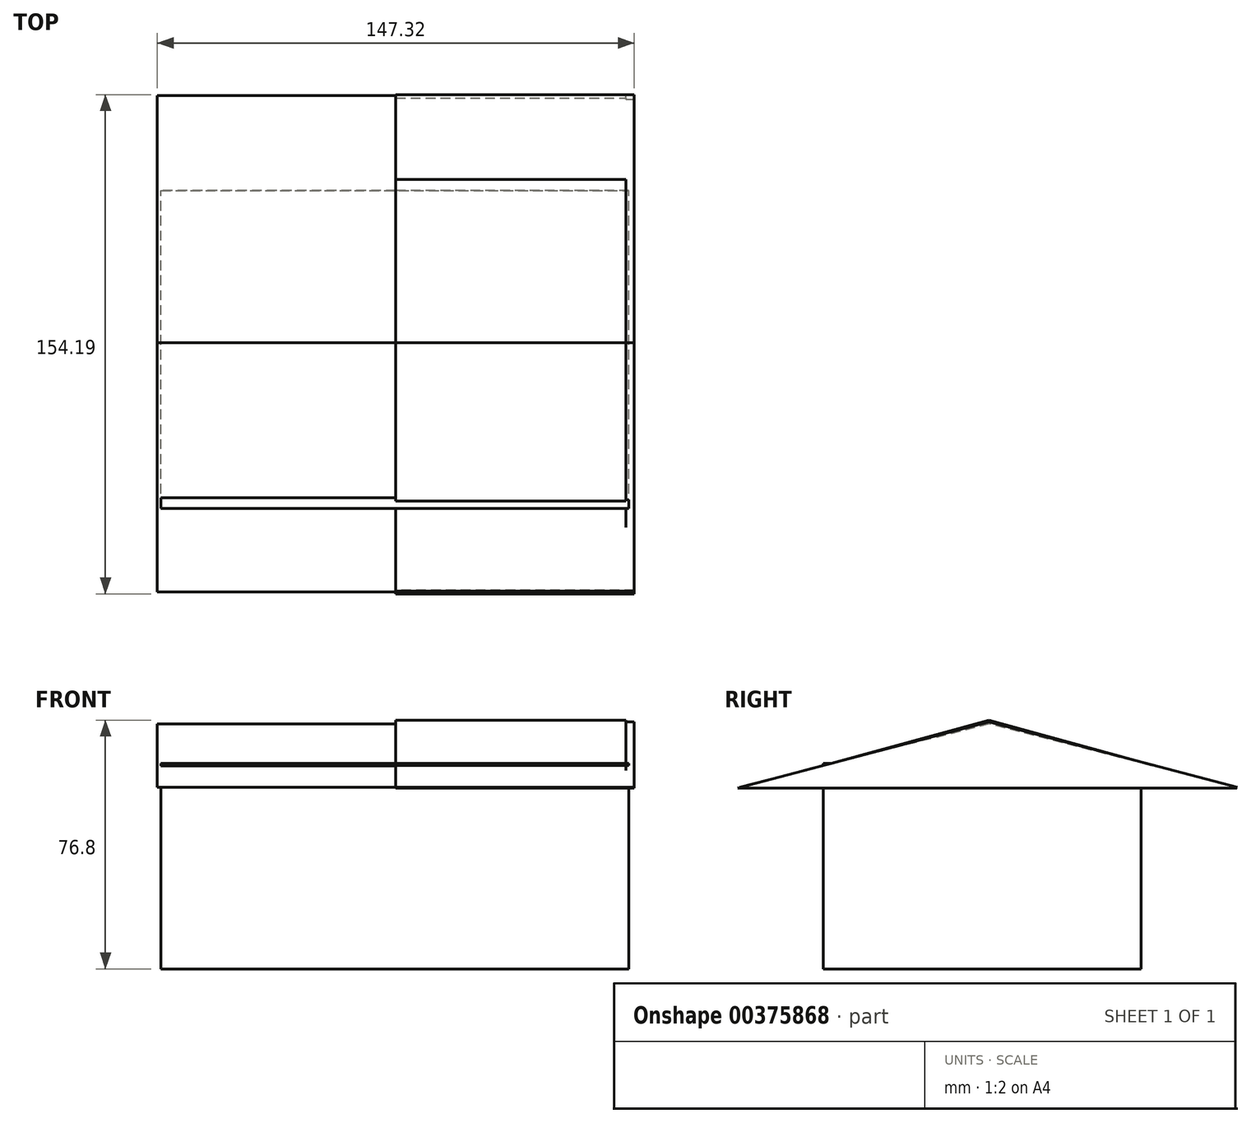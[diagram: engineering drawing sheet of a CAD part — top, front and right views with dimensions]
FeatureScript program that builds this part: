
annotation { "Feature Type Name" : "Feature", "Feature Type Description" : "" }
export const myFeature = defineFeature(function(context is Context, id is Id, definition is map)
    precondition{}
    {
        {
            var Q0;
            Q0=qCreatedBy(makeId("Top.planeOp"),FACE);
            var sketch = newSketch(context, id + "F0", { "sketchPlane" : qUnion([Q0])});
            skLineSegment(sketch, "E0.bottom", {"start": v(-72.58, 47.07) * mm, "end": v(72, 47.07) * mm});
            skLineSegment(sketch, "E0.top", {"start": v(-72.58, -51.15) * mm, "end": v(72, -51.15) * mm});
            skLineSegment(sketch, "E0.left", {"start": v(-72.58, 47.07) * mm, "end": v(-72.58, -51.15) * mm});
            skLineSegment(sketch, "E0.right", {"start": v(72, 47.07) * mm, "end": v(72, -51.15) * mm});
            skSolve(sketch);
        }
        {
            var Q0;
            Q0=makeQuery(id+"F0.imprint","IMPRINT",FACE,{"disambiguationData":[TD([[makeQuery(id+"F0.imprint","IMPRINT",EDGE,{"derivedFrom":sQuery(id+"F0.wireOp",EDGE,"E0.bottom")}),-1.0]])]});
            extrude(context, id + "F1", {"entities" : qUnion([Q0]), "depth" : 63.5 * mm});
        }
        {
            var Q0;
            Q0=qCreatedBy(makeId("Right.planeOp"),FACE);
            var sketch = newSketch(context, id + "F2", { "sketchPlane" : qUnion([Q0])});
            skLineSegment(sketch, "E1", {"start": v(76.4, 55.82) * mm, "end": v(-77.5, 55.82) * mm});
            skLineSegment(sketch, "E2", {"start": v(-77.5, 55.82) * mm, "end": v(0, 76.22) * mm});
            skLineSegment(sketch, "E3", {"start": v(0, 76.22) * mm, "end": v(76.4, 55.82) * mm});
            skSolve(sketch);
        }
        {
            var Q0;
            Q0=makeQuery(id+"F2.imprint","IMPRINT",FACE,{"disambiguationData":[TD([[makeQuery(id+"F2.imprint","IMPRINT",EDGE,{"derivedFrom":sQuery(id+"F2.wireOp",EDGE,"E1")}),-1.0]])]});
            extrude(context, id + "F3", {"entities" : qUnion([Q0]), "operationType" : NewBodyOperationType.ADD, "depth" : 73.66 * mm});
        }
        {
            var Q0;
            Q0=qCreatedBy(makeId("Right.planeOp"),FACE);
            var sketch = newSketch(context, id + "F4", { "sketchPlane" : qUnion([Q0])});
            skLineSegment(sketch, "E4", {"start": v(-76.92, 56.1) * mm, "end": v(76.4, 56.1) * mm});
            skLineSegment(sketch, "E5", {"start": v(76.4, 56.1) * mm, "end": v(0, 75.64) * mm});
            skLineSegment(sketch, "E6", {"start": v(0, 75.64) * mm, "end": v(-76.92, 56.1) * mm});
            skSolve(sketch);
        }
        {
            var Q0;
            Q0 = qSketchRegion(id + "F4", true);
            var Q1;
            {var subQ0=sQuery(id+"F2.wireOp",EDGE,"E2");var subQ1=sQuery(id+"F2.wireOp",EDGE,"E1");var subQ2=sQuery(id+"F0.wireOp",EDGE,"E0.bottom");var subQ3=sQuery(id+"F2.wireOp",EDGE,"E3");Q1=makeQuery(id+"F3.boolean.opBoolean","SPLIT",FACE,{"disambiguationData":[TD([makeQuery(id+"F1.opExtrude","SWEPT_FACE",FACE,{"disambiguationData":[OSD([subQ2])]})])],"derivedFrom":makeQuery(id+"F3.opExtrude","CAP_FACE",FACE,{"disambiguationData":[OSD([subQ1,subQ0,subQ3])],"isStart":false})});}
            var Q2;
            Q2=makeQuery(id+"F1.opExtrude","SWEPT_FACE",FACE,{"disambiguationData":[OSD([sQuery(id+"F0.wireOp",EDGE,"E0.right")])]});
            extrude(context, id + "F5", {"entities" : qUnion([Q0, Q1, Q2]), "operationType" : NewBodyOperationType.ADD, "oppositeDirection" : true, "depth" : 73.66 * mm});
        }
        {
            var Q0;
            Q0=qCreatedBy(makeId("Right.planeOp"),FACE);
            var sketch = newSketch(context, id + "F6", { "sketchPlane" : qUnion([Q0])});
            skLineSegment(sketch, "E7", {"start": v(76.64, 55.82) * mm, "end": v(-76.96, 55.82) * mm});
            skLineSegment(sketch, "E8", {"start": v(-76.96, 55.82) * mm, "end": v(0, 76.8) * mm});
            skLineSegment(sketch, "E9", {"start": v(0, 76.8) * mm, "end": v(76.64, 55.82) * mm});
            skSolve(sketch);
        }
        {
            var Q0;
            Q0=makeQuery(id+"F6.imprint","IMPRINT",FACE,{"disambiguationData":[TD([[makeQuery(id+"F6.imprint","IMPRINT",EDGE,{"derivedFrom":sQuery(id+"F6.wireOp",EDGE,"E7")}),-1.0]])]});
            extrude(context, id + "F7", {"entities" : qUnion([Q0]), "operationType" : NewBodyOperationType.ADD, "depth" : 71.12 * mm});
        }
        {
            var Q0;
            Q0=qCreatedBy(makeId("Right.planeOp"),FACE);
            var sketch = newSketch(context, id + "F8", { "sketchPlane" : qUnion([Q0])});
            skLineSegment(sketch, "E10", {"start": v(-76.63, 56.1) * mm, "end": v(76.68, 56.1) * mm});
            skLineSegment(sketch, "E11", {"start": v(76.68, 56.1) * mm, "end": v(0, 76.22) * mm});
            skLineSegment(sketch, "E12", {"start": v(0, 76.22) * mm, "end": v(-76.63, 56.1) * mm});
            skSolve(sketch);
        }
        {
            var Q0;
            Q0 = qSketchRegion(id + "F8", true);
            var Q1;
            Q1=makeQuery(id+"F5.opExtrude","CAP_FACE",FACE,{"disambiguationData":[OSD([sQuery(id+"F2.wireOp",EDGE,"E1"),sQuery(id+"F2.wireOp",EDGE,"E2"),sQuery(id+"F2.wireOp",EDGE,"E3")])],"isStart":false});
            extrude(context, id + "F9", {"entities" : qUnion([Q0, Q1]), "operationType" : NewBodyOperationType.ADD, "depth" : 73.66 * mm});
        }
    });
